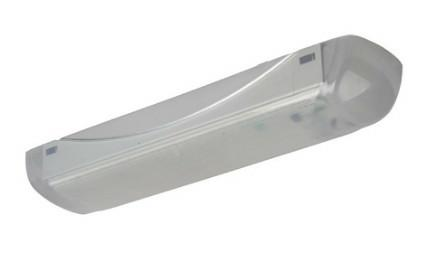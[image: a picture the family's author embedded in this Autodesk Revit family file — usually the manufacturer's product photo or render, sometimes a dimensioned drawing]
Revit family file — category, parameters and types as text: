
# Revit family: GALAD Арго LED
name_source: partatom
category: Осветительные приборы
revit_build: Autodesk Revit 2018 (Build: 20180423_1000(x64)
units: mm (PartAtom-declared; Revit-internal decimal feet)

## family parameters
Источник света = Да
Общий = Нет
Основа = Грань
При загрузке вырезать с полостями = Нет
Размер круглого соединителя = Использовать диаметр
Тип детали = Нормальный
Точка расчета площади = Нет

## types (1)
- GALAD Арго LED-9
    ADSK_Версия Revit = 2018
    ADSK_Версия семейства = 1.01
    ADSK_Единица измерения = шт.
    ADSK_Завод-изготовитель = АО «КАДОШКИНСКИЙ ЭЛЕКТРОТЕХНИЧЕСКИЙ ЗАВОД»
    ADSK_Классификация нагрузок = Освещение
    ADSK_Код изделия = 10618
    ADSK_Количество = 1
    ADSK_Количество фаз = 1
    ADSK_Коэффициент мощности = 0.95
    ADSK_Марка = GALAD Арго LED-9
    ADSK_Масса = 0.5
    ADSK_Масса_Текст = 0.5
    ADSK_Наименование = GALAD Арго LED-9
    ADSK_Наименование краткое = GALAD Арго LED-9
    ADSK_Напряжение = 230 В
    ADSK_Номинальная мощность = 9 В·А
    ADSK_Обозначение = ГОСТ 15150-69
    ADSK_Полная мощность = 9 В·А
    ADSK_Размер_Высота = 45 мм
    ADSK_Размер_Длина = 319 мм
    ADSK_Размер_Ширина = 65 мм
    ADSK_Ток = 0 А
    ADSK_Энергоэффективность = 95 лм/Вт
    IP = 40
    URL = https://galad.ru
    Блок аварийного питания = Нет
    Видимая форма излучения при визуализации = Нет
    Возможный угол наклона = 0
    Группа модели = Светильники
    Диапазон цветовой температуры = 5028±283
    Изготовитель = АО «КАДОШКИНСКИЙ ЭЛЕКТРОТЕХНИЧЕСКИЙ ЗАВОД»
    Излучение по длине прямоугольника = 1219 мм
    Излучение по ширине прямоугольника = 610 мм
    Класс Защиты = 1
    Класс защиты от поражения электрическим током = 1
    Класс светораспределения = П
    Климатическая зона = УХЛ4
    Климатическое исполнение = 1…35 °С
    Коэффициент пульсации = менее 5%
    Материал корпуса = ПММА
    Материал рассеивателя = ПММА
    Неравномерность яркости = 0
    Область использования = ЖКХ
    Описание = Светодиодный светильник GALAD Арго LED укомплектован матовым рассеивателем для минимизации слепящего действия и встроенным блоком питания. Ударопрочное защитное стекло выполнено из светостабилизированного поликарбоната. Установка светильника возможна на стену или на потолок.
    Отметка по умолчанию = 1219 мм
    Полная установленная мощность = 9 В·А
    Световая отдача = 95
    Светофильтр = 16777215
    Смещение цветовой температуры при затухании лампы = <Нет>
    Снижение светового потока во время разгорания = не более 6%
    Срок службы = 12 лет
    Тип КСС = Косинусная
    Тип ПРА = ЭПРА
    Тип источника света = LED
    Тип монтажной поверхности = настенный
    Тип продукции = Светильник
    Тип устройства управления светодиодами = без управления
    Угол наклона = 90.00°
    Файл фотометрической сетки = GALAD argo LED-9.ies
    Цветопередача = 80
    Частота = 50
